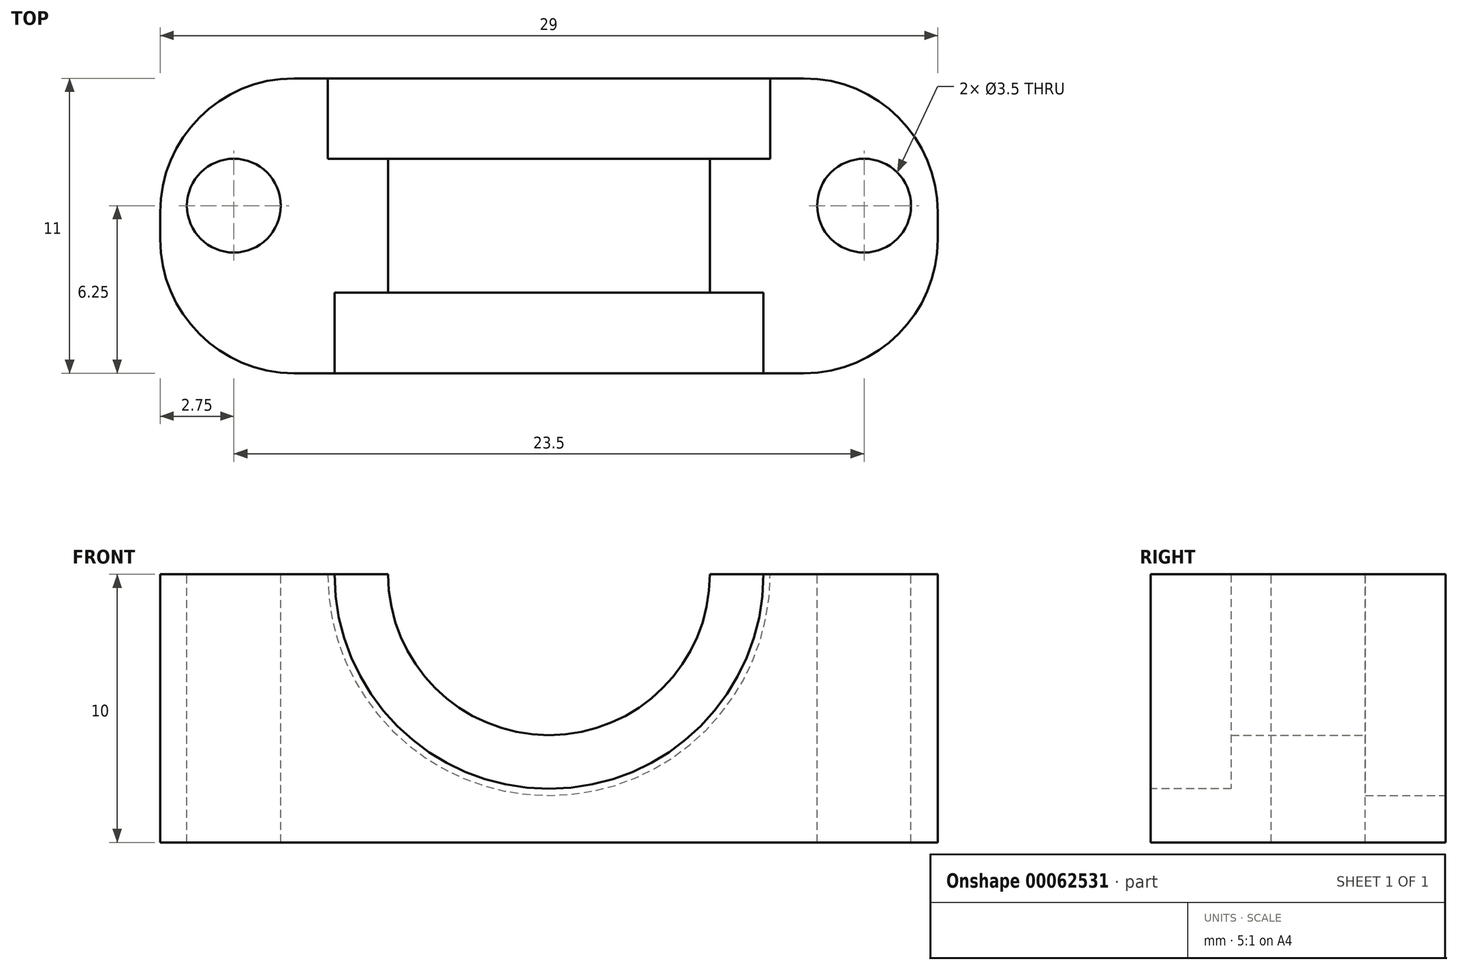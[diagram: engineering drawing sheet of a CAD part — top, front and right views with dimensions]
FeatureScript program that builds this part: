
annotation { "Feature Type Name" : "Feature", "Feature Type Description" : "" }
export const myFeature = defineFeature(function(context is Context, id is Id, definition is map)
    precondition{}
    {
        {
            var Q0;
            Q0=qCreatedBy(makeId("Top.planeOp"),FACE);
            var sketch = newSketch(context, id + "F0", { "sketchPlane" : qUnion([Q0])});
            skLineSegment(sketch, "E0.bottom", {"start": v(0, 0) * mm, "end": v(25, 0) * mm});
            skLineSegment(sketch, "E0.top", {"start": v(0, 11) * mm, "end": v(25, 11) * mm});
            skLineSegment(sketch, "E0.left", {"start": v(0, 0) * mm, "end": v(0, 11) * mm});
            skLineSegment(sketch, "E0.right", {"start": v(25, 0) * mm, "end": v(25, 11) * mm});
            skSolve(sketch);
        }
        {
            var Q0;
            Q0=qSketchRegion(id+"F0",true);
            extrude(context, id + "F1", {"entities" : qUnion([Q0]), "depth" : 10 * mm});
        }
        {
            var Q0;
            Q0=makeQuery(id+"F1.opExtrude","SWEPT_FACE",FACE,{"disambiguationData":[OSD([sQuery(id+"F0.wireOp",EDGE,"E0.bottom")])]});
            var sketch = newSketch(context, id + "F2", { "sketchPlane" : qUnion([Q0])});
            skCircle(sketch, "E1", {"center": v(12.5, 10) * mm, "radius": 8 * mm});
            skSolve(sketch);
        }
        {
            var Q0;
            Q0=qSketchRegion(id+"F2",true);
            extrude(context, id + "F3", {"entities" : qUnion([Q0]), "operationType" : NewBodyOperationType.REMOVE, "oppositeDirection" : true, "depth" : 3 * mm});
        }
        {
            var Q0;
            Q0=makeQuery(id+"F1.opExtrude","SWEPT_FACE",FACE,{"disambiguationData":[OSD([sQuery(id+"F0.wireOp",EDGE,"E0.top")])]});
            var sketch = newSketch(context, id + "F4", { "sketchPlane" : qUnion([Q0])});
            skCircle(sketch, "E2", {"center": v(-12.5, 10) * mm, "radius": 6 * mm});
            skSolve(sketch);
        }
        {
            var Q0;
            Q0=qSketchRegion(id+"F4",true);
            extrude(context, id + "F5", {"entities" : qUnion([Q0]), "operationType" : NewBodyOperationType.REMOVE, "oppositeDirection" : true, "depth" : 9 * mm});
        }
        {
            var Q0;
            Q0=makeQuery(id+"F1.opExtrude","SWEPT_FACE",FACE,{"disambiguationData":[OSD([sQuery(id+"F0.wireOp",EDGE,"E0.left")])]});
            var sketch = newSketch(context, id + "F6", { "sketchPlane" : qUnion([Q0])});
            skLineSegment(sketch, "E3.bottom", {"start": v(-11, 0) * mm, "end": v(0, 0) * mm});
            skLineSegment(sketch, "E3.top", {"start": v(-11, 10) * mm, "end": v(0, 10) * mm});
            skLineSegment(sketch, "E3.left", {"start": v(-11, 0) * mm, "end": v(-11, 10) * mm});
            skLineSegment(sketch, "E3.right", {"start": v(0, 0) * mm, "end": v(0, 10) * mm});
            skSolve(sketch);
        }
        {
            var Q0;
            Q0=qSketchRegion(id+"F6",true);
            extrude(context, id + "F7", {"entities" : qUnion([Q0]), "operationType" : NewBodyOperationType.ADD, "depth" : 2 * mm});
        }
        {
            var Q0;
            Q0=makeQuery(id+"F1.opExtrude","SWEPT_FACE",FACE,{"disambiguationData":[OSD([sQuery(id+"F0.wireOp",EDGE,"E0.right")])]});
            var sketch = newSketch(context, id + "F8", { "sketchPlane" : qUnion([Q0])});
            skLineSegment(sketch, "E4.bottom", {"start": v(11, 10) * mm, "end": v(0, 10) * mm});
            skLineSegment(sketch, "E4.top", {"start": v(11, 0) * mm, "end": v(0, 0) * mm});
            skLineSegment(sketch, "E4.left", {"start": v(11, 10) * mm, "end": v(11, 0) * mm});
            skLineSegment(sketch, "E4.right", {"start": v(0, 10) * mm, "end": v(0, 0) * mm});
            skSolve(sketch);
        }
        {
            var Q0;
            Q0=qSketchRegion(id+"F8",true);
            extrude(context, id + "F9", {"entities" : qUnion([Q0]), "operationType" : NewBodyOperationType.ADD, "depth" : 2 * mm});
        }
        {
            var Q0;
            Q0=makeQuery(id+"F9.opExtrude","CAP_EDGE",EDGE,{"disambiguationData":[OSD([sQuery(id+"F8.wireOp",EDGE,"E4.left")])],"isStart":false});
            var Q1;
            Q1=makeQuery(id+"F9.opExtrude","CAP_EDGE",EDGE,{"disambiguationData":[OSD([sQuery(id+"F8.wireOp",EDGE,"E4.right")])],"isStart":false});
            var Q2;
            Q2=makeQuery(id+"F7.opExtrude","CAP_EDGE",EDGE,{"disambiguationData":[OSD([sQuery(id+"F6.wireOp",EDGE,"E3.left")])],"isStart":false});
            var Q3;
            Q3=makeQuery(id+"F7.opExtrude","CAP_EDGE",EDGE,{"disambiguationData":[OSD([sQuery(id+"F6.wireOp",EDGE,"E3.right")])],"isStart":false});
            fillet(context, id + "F10", {"entities" : qUnion([Q0, Q1, Q2, Q3]), "radius" : 5 * mm, "tangentPropagation" : true, "allowEdgeOverflow" : false});
        }
        {
            var Q0;
            {var subQ0=sQuery(id+"F0.wireOp",EDGE,"E0.bottom");var subQ1=sQuery(id+"F0.wireOp",EDGE,"E0.top");var subQ2=sQuery(id+"F0.wireOp",EDGE,"E0.left");Q0=makeQuery(id+"F5.boolean.opBoolean","SPLIT",FACE,{"disambiguationData":[TD([makeQuery(id+"F1.opExtrude","SWEPT_FACE",FACE,{"disambiguationData":[OSD([subQ2])]})])],"derivedFrom":makeQuery(id+"F1.opExtrude","CAP_FACE",FACE,{"disambiguationData":[OSD([subQ0,subQ1,subQ2,sQuery(id+"F0.wireOp",EDGE,"E0.right")])],"isStart":false})});}
            var sketch = newSketch(context, id + "F11", { "sketchPlane" : qUnion([Q0])});
            skCircle(sketch, "E5", {"center": v(0.75, 6.25) * mm, "radius": 1.75 * mm});
            skCircle(sketch, "E6", {"center": v(24.25, 6.25) * mm, "radius": 1.75 * mm});
            skSolve(sketch);
        }
        {
            var Q0;
            Q0=qSketchRegion(id+"F11",true);
            extrude(context, id + "F12", {"entities" : qUnion([Q0]), "operationType" : NewBodyOperationType.REMOVE, "oppositeDirection" : true, "depth" : 25 * mm});
        }
        {
            var Q0;
            Q0=makeQuery(id+"F9.boolean.opBoolean","MERGE",FACE,{"derivedFrom":[makeQuery(id+"F7.boolean.opBoolean","MERGE",FACE,{"derivedFrom":[makeQuery(id+"F1.opExtrude","SWEPT_FACE",FACE,{"disambiguationData":[OSD([sQuery(id+"F0.wireOp",EDGE,"E0.top")])]}),makeQuery(id+"F7.opExtrude","SWEPT_FACE",FACE,{"disambiguationData":[OSD([sQuery(id+"F6.wireOp",EDGE,"E3.left")])]})]}),makeQuery(id+"F9.opExtrude","SWEPT_FACE",FACE,{"disambiguationData":[OSD([sQuery(id+"F8.wireOp",EDGE,"E4.left")])]})]});
            var sketch = newSketch(context, id + "F13", { "sketchPlane" : qUnion([Q0])});
            skCircle(sketch, "E7", {"center": v(-12.5, 10) * mm, "radius": 8.25 * mm});
            skSolve(sketch);
        }
        {
            var Q0;
            Q0 = qSketchRegion(id + "F13", true);
            extrude(context, id + "F14", {"entities" : qUnion([Q0]), "operationType" : NewBodyOperationType.REMOVE, "oppositeDirection" : true, "depth" : 3 * mm});
        }
    });
